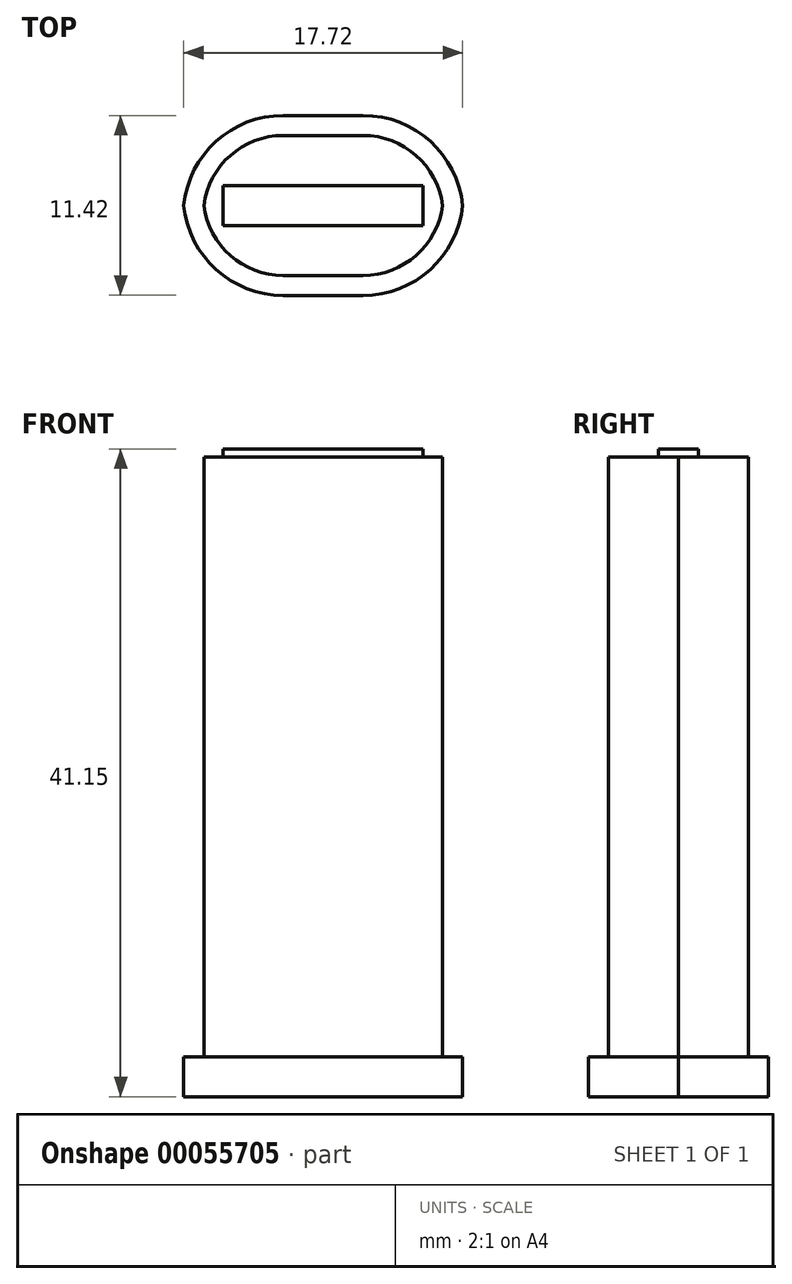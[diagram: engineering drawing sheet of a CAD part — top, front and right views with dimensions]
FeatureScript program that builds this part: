
annotation { "Feature Type Name" : "Feature", "Feature Type Description" : "" }
export const myFeature = defineFeature(function(context is Context, id is Id, definition is map)
    precondition{}
    {
        {
            var Q0;
            Q0=qCreatedBy(makeId("Top.planeOp"),FACE);
            var sketch = newSketch(context, id + "F0", { "sketchPlane" : qUnion([Q0])});
            skLineSegment(sketch, "E0.rect.bottom", {"start": v(2.54, -4.44) * mm, "end": v(-2.54, -4.45) * mm});
            skLineSegment(sketch, "E0.rect.top", {"start": v(2.54, 4.45) * mm, "end": v(-2.54, 4.45) * mm});
            skLineSegment(sketch, "E0.rect.left", {"start": v(7.62, -0.63) * mm, "end": v(7.62, 0.64) * mm});
            skLineSegment(sketch, "E0.rect.right", {"start": v(-7.62, -0.64) * mm, "end": v(-7.62, 0.63) * mm});
            skPoint(sketch, "E0.rect.middle", {"position": v(0, 0) * mm});
            skPoint(sketch, "E1.visualSharp", {"position": v(-7.62, 4.44) * mm});
            skArc(sketch, "E1.filletArc", {"start": v(-2.54, 4.45) * mm, "mid": v(-6.13, 2.96) * mm, "end": v(-7.62, -0.64) * mm});
            skPoint(sketch, "E2.visualSharp", {"position": v(-7.62, -4.45) * mm});
            skArc(sketch, "E2.filletArc", {"start": v(-7.62, 0.64) * mm, "mid": v(-6.13, -2.96) * mm, "end": v(-2.54, -4.45) * mm});
            skPoint(sketch, "E3.visualSharp", {"position": v(7.62, 4.45) * mm});
            skArc(sketch, "E3.filletArc", {"start": v(7.62, -0.63) * mm, "mid": v(6.13, 2.96) * mm, "end": v(2.54, 4.45) * mm});
            skPoint(sketch, "E4.visualSharp", {"position": v(7.62, -4.44) * mm});
            skArc(sketch, "E4.filletArc", {"start": v(2.54, -4.45) * mm, "mid": v(6.13, -2.96) * mm, "end": v(7.62, 0.64) * mm});
            skLineSegment(sketch, "E5.rect.bottom", {"start": v(6.35, -1.27) * mm, "end": v(-6.35, -1.27) * mm});
            skLineSegment(sketch, "E5.rect.top", {"start": v(6.35, 1.27) * mm, "end": v(-6.35, 1.27) * mm});
            skLineSegment(sketch, "E5.rect.left", {"start": v(6.35, -1.27) * mm, "end": v(6.35, 1.27) * mm});
            skLineSegment(sketch, "E5.rect.right", {"start": v(-6.35, -1.27) * mm, "end": v(-6.35, 1.27) * mm});
            skLineSegment(sketch, "E6.bottom", {"start": v(2.54, -5.72) * mm, "end": v(-2.54, -5.72) * mm});
            skLineSegment(sketch, "E6.top", {"start": v(2.54, 5.72) * mm, "end": v(-2.54, 5.72) * mm});
            skLineSegment(sketch, "E6.left", {"start": v(8.89, -0.63) * mm, "end": v(8.89, 0.64) * mm});
            skLineSegment(sketch, "E6.right", {"start": v(-8.9, -0.63) * mm, "end": v(-8.9, 0.64) * mm});
            skPoint(sketch, "E7.visualSharp", {"position": v(-8.9, 5.72) * mm});
            skArc(sketch, "E7.filletArc", {"start": v(-2.54, 5.72) * mm, "mid": v(-7.03, 3.86) * mm, "end": v(-8.9, -0.64) * mm});
            skPoint(sketch, "E8.visualSharp", {"position": v(-8.89, -5.72) * mm});
            skArc(sketch, "E8.filletArc", {"start": v(-8.89, -5.2) * mm, "mid": v(-8.74, -5.57) * mm, "end": v(-8.38, -5.72) * mm});
            skArc(sketch, "E9.filletArc", {"start": v(-8.9, 0.64) * mm, "mid": v(-7.03, -3.86) * mm, "end": v(-2.54, -5.71) * mm});
            skPoint(sketch, "E10.visualSharp", {"position": v(8.9, -5.72) * mm});
            skArc(sketch, "E10.filletArc", {"start": v(2.54, -5.72) * mm, "mid": v(7.03, -3.86) * mm, "end": v(8.89, 0.64) * mm});
            skPoint(sketch, "E11.visualSharp", {"position": v(8.89, 5.72) * mm});
            skArc(sketch, "E11.filletArc", {"start": v(8.9, -0.63) * mm, "mid": v(7.03, 3.86) * mm, "end": v(2.54, 5.72) * mm});
            skSolve(sketch);
        }
        {
            var Q0;
            Q0=makeQuery(id+"F0.imprint","IMPRINT",FACE,{"disambiguationData":[TD([[makeQuery(id+"F0.imprint","IMPRINT",EDGE,{"derivedFrom":sQuery(id+"F0.wireOp",EDGE,"E5.rect.bottom")}),-1.0]])]});
            extrude(context, id + "F1", {"entities" : qUnion([Q0]), "depth" : 38.6 * mm});
        }
        {
            var Q0;
            Q0=makeQuery(id+"F0.imprint","IMPRINT",FACE,{"disambiguationData":[TD([[makeQuery(id+"F0.imprint","IMPRINT",EDGE,{"derivedFrom":sQuery(id+"F0.wireOp",EDGE,"E0.rect.bottom")}),-1.0]])]});
            var Q1;
            Q1=makeQuery(id+"F0.imprint","IMPRINT",FACE,{"disambiguationData":[TD([[makeQuery(id+"F0.imprint","IMPRINT",EDGE,{"derivedFrom":sQuery(id+"F0.wireOp",EDGE,"E5.rect.bottom")}),-1.0]])]});
            extrude(context, id + "F2", {"entities" : qUnion([Q0, Q1]), "depth" : 38.1 * mm});
        }
        {
            var Q0;
            {var subQ1=sQuery(id+"F0.wireOp",EDGE,"E0.rect.bottom");Q0=makeQuery(id+"F0.imprint","IMPRINT",FACE,{"disambiguationData":[TD([[makeQuery(id+"F0.imprint","IMPRINT",EDGE,{"derivedFrom":subQ1}),1.0]])]});}
            var Q1;
            {var subQ1=sQuery(id+"F0.wireOp",EDGE,"E0.rect.bottom");Q1=makeQuery(id+"F0.imprint","IMPRINT",FACE,{"disambiguationData":[TD([[makeQuery(id+"F0.imprint","IMPRINT",EDGE,{"derivedFrom":subQ1}),-1.0]])]});}
            var Q2;
            Q2=makeQuery(id+"F0.imprint","IMPRINT",FACE,{"disambiguationData":[TD([[makeQuery(id+"F0.imprint","IMPRINT",EDGE,{"derivedFrom":sQuery(id+"F0.wireOp",EDGE,"E5.rect.bottom")}),-1.0]])]});
            var Q3;
            {var subQ0=sQuery(id+"F0.wireOp",EDGE,"E0.rect.left");Q3=makeQuery(id+"F0.imprint","IMPRINT",FACE,{"disambiguationData":[TD([[makeQuery(id+"F0.imprint","IMPRINT",EDGE,{"derivedFrom":subQ0}),1.0]])]});}
            var Q4;
            {var subQ0=sQuery(id+"F0.wireOp",EDGE,"E0.rect.right");Q4=makeQuery(id+"F0.imprint","IMPRINT",FACE,{"disambiguationData":[TD([[makeQuery(id+"F0.imprint","IMPRINT",EDGE,{"derivedFrom":subQ0}),-1.0]])]});}
            extrude(context, id + "F3", {"entities" : qUnion([Q0, Q1, Q2, Q3, Q4]), "operationType" : NewBodyOperationType.ADD, "oppositeDirection" : true, "depth" : 2.54 * mm});
        }
    });
